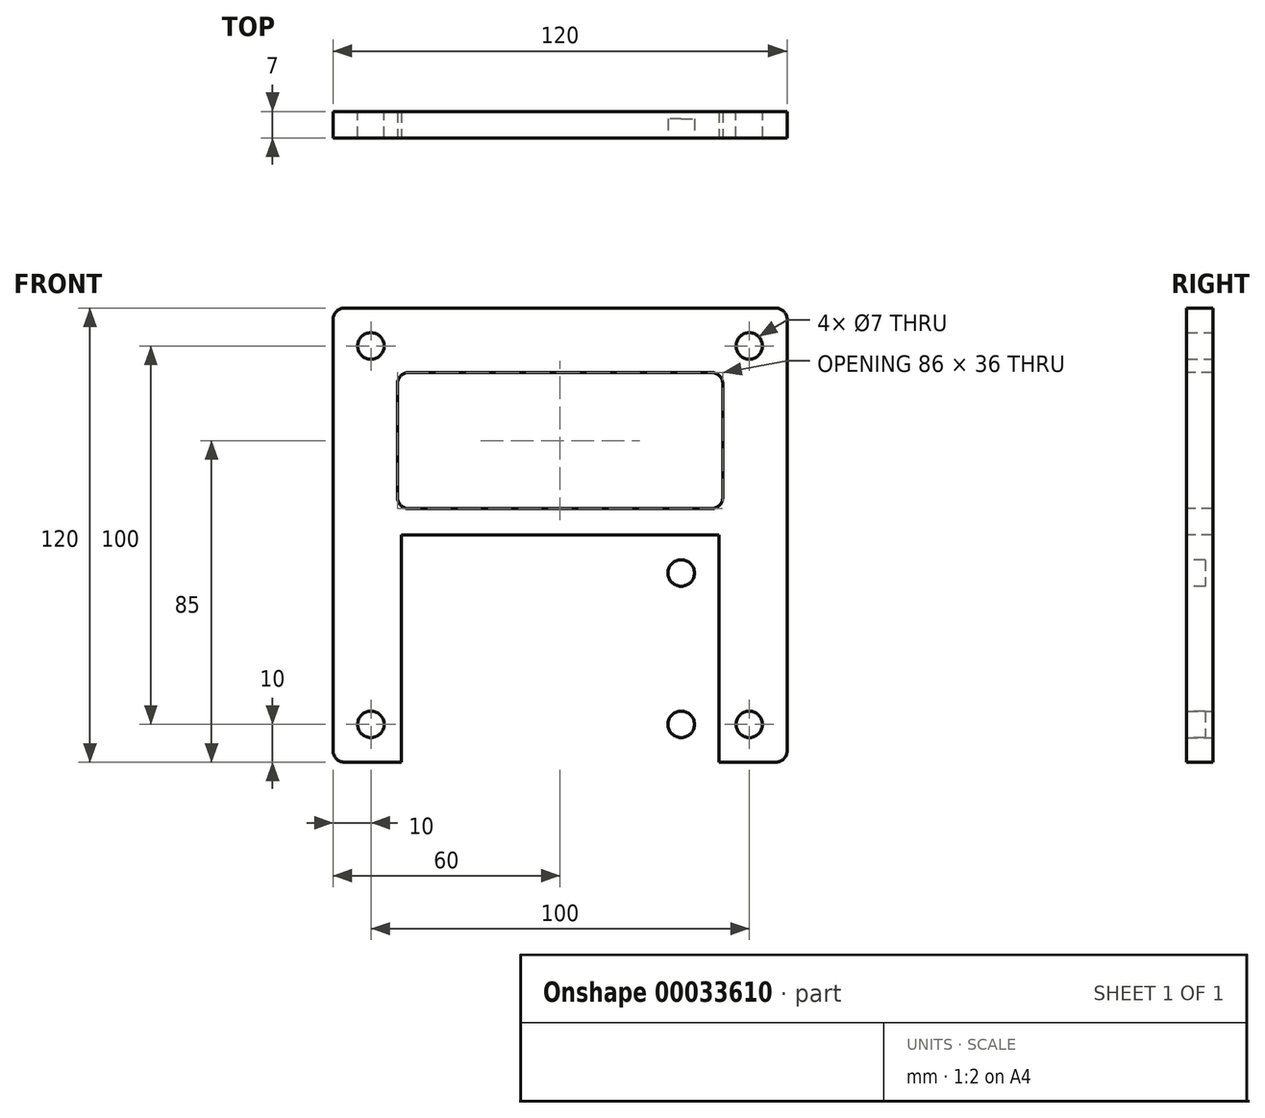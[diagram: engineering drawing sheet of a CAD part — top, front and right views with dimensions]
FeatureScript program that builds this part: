
annotation { "Feature Type Name" : "Feature", "Feature Type Description" : "" }
export const myFeature = defineFeature(function(context is Context, id is Id, definition is map)
    precondition{}
    {
        {
            var Q0;
            Q0=qCreatedBy(makeId("Front.planeOp"),FACE);
            var sketch = newSketch(context, id + "F0", { "sketchPlane" : qUnion([Q0])});
            skPoint(sketch, "E0.rect.middle", {"position": v(0, 0) * mm});
            skCircle(sketch, "E1", {"center": v(-50, 50) * mm, "radius": 3.5 * mm});
            skCircle(sketch, "E2", {"center": v(50, 50) * mm, "radius": 3.5 * mm});
            skCircle(sketch, "E3", {"center": v(-50, -50) * mm, "radius": 3.5 * mm});
            skCircle(sketch, "E4", {"center": v(50, -50) * mm, "radius": 3.5 * mm});
            skLineSegment(sketch, "E5.rect.bottom", {"start": v(57, -60) * mm, "end": v(-57, -60) * mm});
            skLineSegment(sketch, "E5.rect.top", {"start": v(57, 60) * mm, "end": v(-57, 60) * mm});
            skLineSegment(sketch, "E5.rect.left", {"start": v(60, -57) * mm, "end": v(60, 57) * mm});
            skLineSegment(sketch, "E5.rect.right", {"start": v(-60, -57) * mm, "end": v(-60, 57) * mm});
            skPoint(sketch, "E6.visualSharp", {"position": v(-60, 60) * mm});
            skArc(sketch, "E6.filletArc", {"start": v(-57, 60) * mm, "mid": v(-59.12, 59.12) * mm, "end": v(-60, 57) * mm});
            skPoint(sketch, "E7.visualSharp", {"position": v(60, 60) * mm});
            skArc(sketch, "E7.filletArc", {"start": v(60, 57) * mm, "mid": v(59.12, 59.12) * mm, "end": v(57, 60) * mm});
            skPoint(sketch, "E8.visualSharp", {"position": v(60, -60) * mm});
            skArc(sketch, "E8.filletArc", {"start": v(57, -60) * mm, "mid": v(59.12, -59.12) * mm, "end": v(60, -57) * mm});
            skPoint(sketch, "E9.visualSharp", {"position": v(-60, -60) * mm});
            skArc(sketch, "E9.filletArc", {"start": v(-60, -57) * mm, "mid": v(-59.12, -59.12) * mm, "end": v(-57, -60) * mm});
            skSolve(sketch);
        }
        {
            var Q0;
            Q0 = qSketchRegion(id + "F0", true);
            extrude(context, id + "F1", {"entities" : qUnion([Q0]), "depth" : 7 * mm});
        }
        {
            var Q0;
            Q0=makeQuery(id+"F1.opExtrude","CAP_FACE",FACE,{"disambiguationData":[OSD([sQuery(id+"F0.wireOp",EDGE,"E1"),sQuery(id+"F0.wireOp",EDGE,"E2"),sQuery(id+"F0.wireOp",EDGE,"E3"),sQuery(id+"F0.wireOp",EDGE,"E4"),sQuery(id+"F0.wireOp",EDGE,"E5.rect.bottom"),sQuery(id+"F0.wireOp",EDGE,"E5.rect.top"),sQuery(id+"F0.wireOp",EDGE,"E5.rect.left"),sQuery(id+"F0.wireOp",EDGE,"E5.rect.right"),sQuery(id+"F0.wireOp",EDGE,"E6.filletArc"),sQuery(id+"F0.wireOp",EDGE,"E7.filletArc"),sQuery(id+"F0.wireOp",EDGE,"E8.filletArc"),sQuery(id+"F0.wireOp",EDGE,"E9.filletArc")])],"isStart":false});
            var sketch = newSketch(context, id + "F2", { "sketchPlane" : qUnion([Q0])});
            skLineSegment(sketch, "E10.left", {"start": v(-42, 0) * mm, "end": v(-42, -60) * mm});
            skCircle(sketch, "E11", {"center": v(-32, -50) * mm, "radius": 3.5 * mm});
            skCircle(sketch, "E12", {"center": v(-32, -10) * mm, "radius": 3.5 * mm});
            skLineSegment(sketch, "E13", {"start": v(-42, 0) * mm, "end": v(0, 0) * mm});
            skLineSegment(sketch, "E14", {"start": v(-42, -60) * mm, "end": v(0, -60) * mm});
            skLineSegment(sketch, "E15.MirrorCS", {"start": v(42, 0) * mm, "end": v(0, 0) * mm});
            skLineSegment(sketch, "E16.MirrorCS", {"start": v(42, 0) * mm, "end": v(42, -60) * mm});
            skCircle(sketch, "E17.MirrorC", {"center": v(32, -10) * mm, "radius": 3.5 * mm});
            skCircle(sketch, "E18.MirrorC", {"center": v(32, -50) * mm, "radius": 3.5 * mm});
            skLineSegment(sketch, "E19.MirrorCS", {"start": v(42, -60) * mm, "end": v(0, -60) * mm});
            skSolve(sketch);
        }
        {
            var Q0;
            Q0=makeQuery(id+"F2.imprint","IMPRINT",FACE,{"disambiguationData":[TD([[makeQuery(id+"F2.imprint","IMPRINT",EDGE,{"derivedFrom":sQuery(id+"F2.wireOp",EDGE,"E12")}),1.0]])]});
            var Q1;
            Q1=makeQuery(id+"F2.imprint","IMPRINT",FACE,{"disambiguationData":[TD([[makeQuery(id+"F2.imprint","IMPRINT",EDGE,{"derivedFrom":sQuery(id+"F2.wireOp",EDGE,"E11")}),1.0]])]});
            var Q2;
            Q2=makeQuery(id+"F2.imprint","IMPRINT",FACE,{"disambiguationData":[TD([[makeQuery(id+"F2.imprint","IMPRINT",EDGE,{"derivedFrom":sQuery(id+"F2.wireOp",EDGE,"E18.MirrorC")}),-1.0]])]});
            var Q3;
            Q3=makeQuery(id+"F2.imprint","IMPRINT",FACE,{"disambiguationData":[TD([[makeQuery(id+"F2.imprint","IMPRINT",EDGE,{"derivedFrom":sQuery(id+"F2.wireOp",EDGE,"E17.MirrorC")}),-1.0]])]});
            extrude(context, id + "F3", {"entities" : qUnion([Q0, Q1, Q2, Q3]), "operationType" : NewBodyOperationType.REMOVE, "oppositeDirection" : true, "depth" : 25 * mm});
        }
        {
            var Q0;
            Q0=makeQuery(id+"F1.opExtrude","CAP_FACE",FACE,{"disambiguationData":[OSD([sQuery(id+"F0.wireOp",EDGE,"E1"),sQuery(id+"F0.wireOp",EDGE,"E2"),sQuery(id+"F0.wireOp",EDGE,"E3"),sQuery(id+"F0.wireOp",EDGE,"E4"),sQuery(id+"F0.wireOp",EDGE,"E5.rect.bottom"),sQuery(id+"F0.wireOp",EDGE,"E5.rect.top"),sQuery(id+"F0.wireOp",EDGE,"E5.rect.left"),sQuery(id+"F0.wireOp",EDGE,"E5.rect.right"),sQuery(id+"F0.wireOp",EDGE,"E6.filletArc"),sQuery(id+"F0.wireOp",EDGE,"E7.filletArc"),sQuery(id+"F0.wireOp",EDGE,"E8.filletArc"),sQuery(id+"F0.wireOp",EDGE,"E9.filletArc")])],"isStart":true});
            var sketch = newSketch(context, id + "F4", { "sketchPlane" : qUnion([Q0])});
            skCircle(sketch, "E20", {"center": v(-32, -10) * mm, "radius": 5.5 * mm});
            skCircle(sketch, "E21", {"center": v(-32, -50) * mm, "radius": 5.5 * mm});
            skCircle(sketch, "E22", {"center": v(32, -50) * mm, "radius": 5.5 * mm});
            skCircle(sketch, "E23", {"center": v(32, -10) * mm, "radius": 5.5 * mm});
            skSolve(sketch);
        }
        {
            var Q0;
            Q0 = qSketchRegion(id + "F4", true);
            extrude(context, id + "F5", {"entities" : qUnion([Q0]), "operationType" : NewBodyOperationType.REMOVE, "oppositeDirection" : true, "depth" : 2 * mm});
        }
        {
            var Q0;
            Q0=makeQuery(id+"F1.opExtrude","CAP_FACE",FACE,{"disambiguationData":[OSD([sQuery(id+"F0.wireOp",EDGE,"E1"),sQuery(id+"F0.wireOp",EDGE,"E2"),sQuery(id+"F0.wireOp",EDGE,"E3"),sQuery(id+"F0.wireOp",EDGE,"E4"),sQuery(id+"F0.wireOp",EDGE,"E5.rect.bottom"),sQuery(id+"F0.wireOp",EDGE,"E5.rect.top"),sQuery(id+"F0.wireOp",EDGE,"E5.rect.left"),sQuery(id+"F0.wireOp",EDGE,"E5.rect.right"),sQuery(id+"F0.wireOp",EDGE,"E6.filletArc"),sQuery(id+"F0.wireOp",EDGE,"E7.filletArc"),sQuery(id+"F0.wireOp",EDGE,"E8.filletArc"),sQuery(id+"F0.wireOp",EDGE,"E9.filletArc")])],"isStart":false});
            var sketch = newSketch(context, id + "F6", { "sketchPlane" : qUnion([Q0])});
            skLineSegment(sketch, "E24", {"start": v(-60, 7) * mm, "end": v(60, 7) * mm, "construction": true});
            skLineSegment(sketch, "E25", {"start": v(-60, 43) * mm, "end": v(60, 43) * mm, "construction": true});
            skLineSegment(sketch, "E26", {"start": v(-43, 60) * mm, "end": v(-43, 7) * mm, "construction": true});
            skLineSegment(sketch, "E27", {"start": v(43, 60) * mm, "end": v(43, 7) * mm, "construction": true});
            skLineSegment(sketch, "E28.bottom", {"start": v(-43, 43) * mm, "end": v(43, 43) * mm});
            skLineSegment(sketch, "E28.top", {"start": v(-43, 7) * mm, "end": v(43, 7) * mm});
            skLineSegment(sketch, "E28.left", {"start": v(-43, 43) * mm, "end": v(-43, 7) * mm});
            skLineSegment(sketch, "E28.right", {"start": v(43, 43) * mm, "end": v(43, 7) * mm});
            skSolve(sketch);
        }
        {
            var Q0;
            Q0 = qSketchRegion(id + "F6", true);
            extrude(context, id + "F7", {"entities" : qUnion([Q0]), "operationType" : NewBodyOperationType.REMOVE, "oppositeDirection" : true, "depth" : 25 * mm});
        }
        {
            var Q0;
            Q0=makeQuery(id+"F7.boolean.opBoolean","COPY",EDGE,{"derivedFrom":makeQuery(id+"F7.opExtrude","SWEPT_EDGE",EDGE,{"disambiguationData":[OSD([sQuery(id+"F6.wireOp",EDGE,"E28.bottom"),sQuery(id+"F6.wireOp",EDGE,"E28.left")])]})});
            var Q1;
            Q1=makeQuery(id+"F7.boolean.opBoolean","COPY",EDGE,{"derivedFrom":makeQuery(id+"F7.opExtrude","SWEPT_EDGE",EDGE,{"disambiguationData":[OSD([sQuery(id+"F6.wireOp",EDGE,"E28.top"),sQuery(id+"F6.wireOp",EDGE,"E28.left")])]})});
            var Q2;
            Q2=makeQuery(id+"F7.boolean.opBoolean","COPY",EDGE,{"derivedFrom":makeQuery(id+"F7.opExtrude","SWEPT_EDGE",EDGE,{"disambiguationData":[OSD([sQuery(id+"F6.wireOp",EDGE,"E28.bottom"),sQuery(id+"F6.wireOp",EDGE,"E28.right")])]})});
            var Q3;
            Q3=makeQuery(id+"F7.boolean.opBoolean","COPY",EDGE,{"derivedFrom":makeQuery(id+"F7.opExtrude","SWEPT_EDGE",EDGE,{"disambiguationData":[OSD([sQuery(id+"F6.wireOp",EDGE,"E28.top"),sQuery(id+"F6.wireOp",EDGE,"E28.right")])]})});
            fillet(context, id + "F8", {"entities" : qUnion([Q0, Q1, Q2, Q3]), "radius" : 3 * mm, "tangentPropagation" : true, "allowEdgeOverflow" : false});
        }
    });
